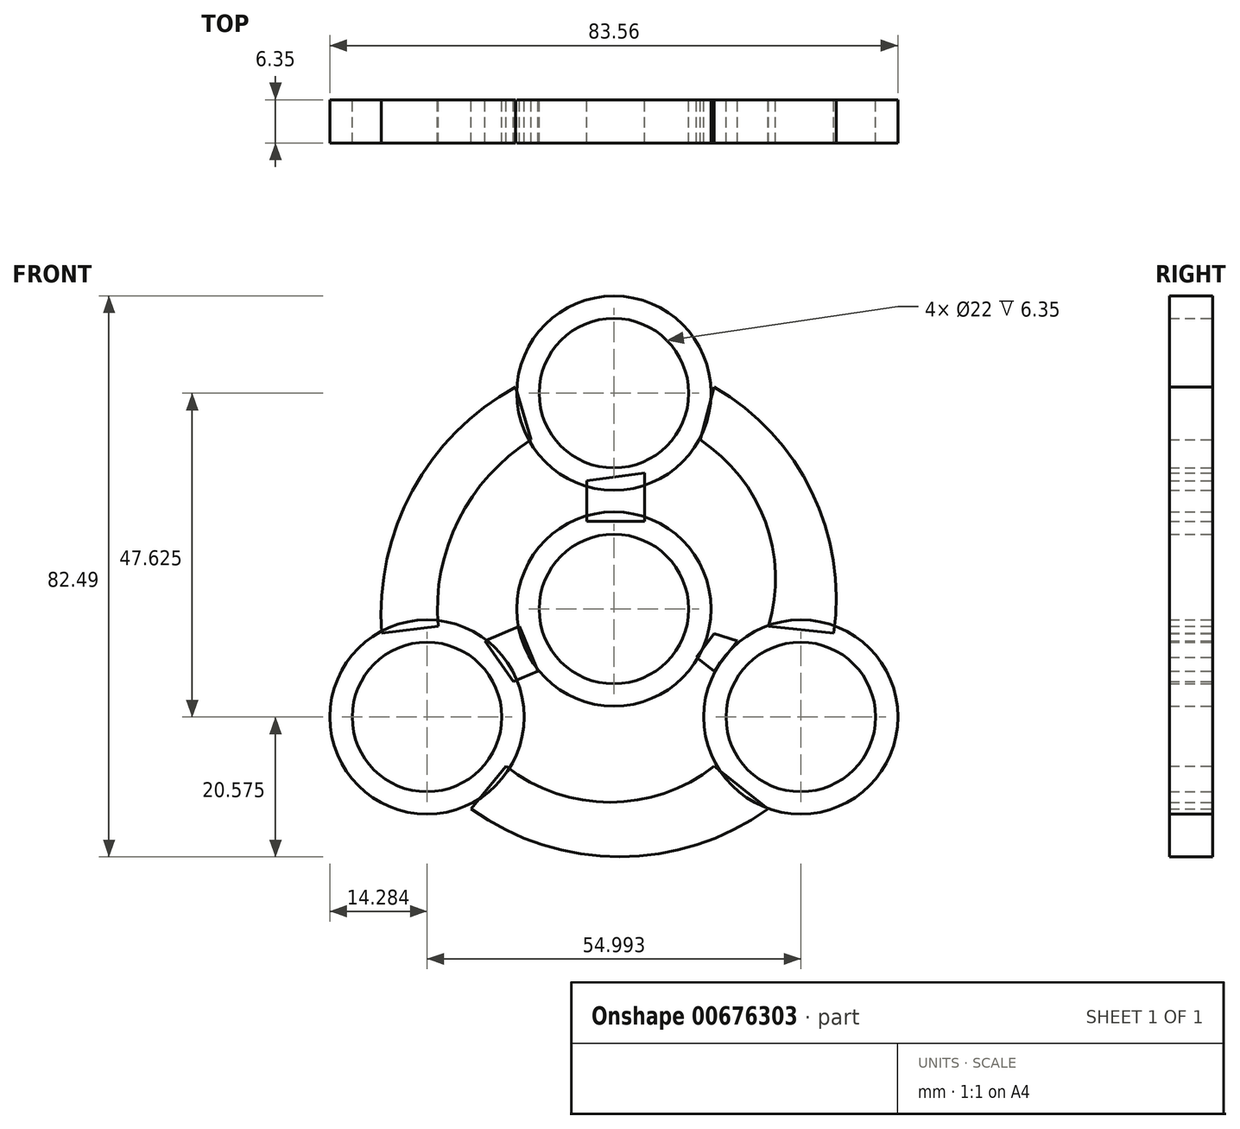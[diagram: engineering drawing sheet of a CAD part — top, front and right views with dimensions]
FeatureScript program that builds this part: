
annotation { "Feature Type Name" : "Feature", "Feature Type Description" : "" }
export const myFeature = defineFeature(function(context is Context, id is Id, definition is map)
    precondition{}
    {
        {
            var Q0;
            Q0=qCreatedBy(makeId("Front.planeOp"),FACE);
            var sketch = newSketch(context, id + "F0", { "sketchPlane" : qUnion([Q0])});
            skCircle(sketch, "E0", {"center": v(0, 0) * mm, "radius": 14.29 * mm});
            skCircle(sketch, "E1", {"center": v(0, 0) * mm, "radius": 11 * mm});
            skLineSegment(sketch, "E2", {"start": v(0, 0) * mm, "end": v(0, 31.75) * mm});
            skCircle(sketch, "E3", {"center": v(0, 31.75) * mm, "radius": 14.29 * mm});
            skCircle(sketch, "E4", {"center": v(0, 31.75) * mm, "radius": 11 * mm});
            skCircle(sketch, "E5.1.0", {"center": v(-27.5, -15.87) * mm, "radius": 14.29 * mm});
            skCircle(sketch, "E5.1.1", {"center": v(-27.5, -15.87) * mm, "radius": 11 * mm});
            skCircle(sketch, "E5.2.0", {"center": v(27.5, -15.88) * mm, "radius": 14.29 * mm});
            skCircle(sketch, "E5.2.1", {"center": v(27.5, -15.88) * mm, "radius": 11 * mm});
            skSolve(sketch);
        }
        {
            var Q0;
            Q0=qCreatedBy(makeId("Front.planeOp"),FACE);
            var sketch = newSketch(context, id + "F1", { "sketchPlane" : qUnion([Q0])});
            skArc(sketch, "E6", {"start": v(-14.49, 32.64) * mm, "mid": v(-29.64, 17.42) * mm, "end": v(-34.15, -3.57) * mm});
            skArc(sketch, "E7", {"start": v(-12.16, 24.88) * mm, "mid": v(-22.86, 13.1) * mm, "end": v(-25.87, -2.54) * mm});
            skArc(sketch, "E8", {"start": v(22.76, -2.54) * mm, "mid": v(22.29, 12.85) * mm, "end": v(12.68, 24.88) * mm});
            skArc(sketch, "E9", {"start": v(32.33, -3.57) * mm, "mid": v(29.11, 17.24) * mm, "end": v(14.74, 32.64) * mm});
            skArc(sketch, "E10", {"start": v(-15.89, -23.12) * mm, "mid": v(-0.57, -28.42) * mm, "end": v(14.75, -23.12) * mm});
            skArc(sketch, "E11", {"start": v(-21, -29.37) * mm, "mid": v(0.85, -36.45) * mm, "end": v(22.7, -29.37) * mm});
            skLineSegment(sketch, "E12", {"start": v(-3.97, 18.87) * mm, "end": v(-3.97, 12.9) * mm});
            skLineSegment(sketch, "E13", {"start": v(-3.97, 12.9) * mm, "end": v(4.54, 12.9) * mm});
            skLineSegment(sketch, "E14", {"start": v(4.54, 12.9) * mm, "end": v(4.54, 20) * mm});
            skLineSegment(sketch, "E15", {"start": v(4.54, 20) * mm, "end": v(-3.97, 18.87) * mm});
            skLineSegment(sketch, "E16", {"start": v(-19, -4.68) * mm, "end": v(-13.9, -2.54) * mm});
            skLineSegment(sketch, "E17", {"start": v(-13.9, -2.54) * mm, "end": v(-11.14, -9.12) * mm});
            skLineSegment(sketch, "E18", {"start": v(-11.14, -9.12) * mm, "end": v(-14.8, -10.65) * mm});
            skLineSegment(sketch, "E19", {"start": v(-14.8, -10.65) * mm, "end": v(-19, -4.68) * mm});
            skLineSegment(sketch, "E20", {"start": v(14.75, -3.61) * mm, "end": v(18.16, -4.68) * mm});
            skLineSegment(sketch, "E21", {"start": v(18.16, -4.68) * mm, "end": v(14.75, -9.12) * mm});
            skLineSegment(sketch, "E22", {"start": v(14.75, -9.12) * mm, "end": v(12.16, -7.12) * mm});
            skLineSegment(sketch, "E23", {"start": v(12.16, -7.12) * mm, "end": v(14.75, -3.61) * mm});
            skLineSegment(sketch, "E24", {"start": v(-34.15, -3.57) * mm, "end": v(-25.87, -2.54) * mm});
            skLineSegment(sketch, "E25", {"start": v(-14.49, 32.64) * mm, "end": v(-12.16, 24.88) * mm});
            skLineSegment(sketch, "E26", {"start": v(12.68, 24.88) * mm, "end": v(14.74, 32.64) * mm});
            skLineSegment(sketch, "E27", {"start": v(22.76, -2.54) * mm, "end": v(32.33, -3.57) * mm});
            skLineSegment(sketch, "E28", {"start": v(-21, -29.37) * mm, "end": v(-15.89, -23.12) * mm});
            skLineSegment(sketch, "E29", {"start": v(14.75, -23.12) * mm, "end": v(22.7, -29.37) * mm});
            skSolve(sketch);
        }
        {
            var Q0;
            Q0=makeQuery(id+"F1.imprint","IMPRINT",FACE,{"disambiguationData":[TD([[makeQuery(id+"F1.imprint","IMPRINT",EDGE,{"derivedFrom":sQuery(id+"F1.wireOp",EDGE,"E6")}),1.0]])]});
            var Q1;
            Q1=makeQuery(id+"F1.imprint","IMPRINT",FACE,{"disambiguationData":[TD([[makeQuery(id+"F1.imprint","IMPRINT",EDGE,{"derivedFrom":sQuery(id+"F1.wireOp",EDGE,"E8")}),-1.0]])]});
            var Q2;
            Q2=makeQuery(id+"F0.imprint","IMPRINT",FACE,{"disambiguationData":[TD([[makeQuery(id+"F0.imprint","IMPRINT",EDGE,{"derivedFrom":sQuery(id+"F0.wireOp",EDGE,"E5.2.0")}),1.0]])]});
            var Q3;
            Q3=makeQuery(id+"F1.imprint","IMPRINT",FACE,{"disambiguationData":[TD([[makeQuery(id+"F1.imprint","IMPRINT",EDGE,{"derivedFrom":sQuery(id+"F1.wireOp",EDGE,"E20")}),-1.0]])]});
            var Q4;
            Q4=makeQuery(id+"F0.imprint","IMPRINT",FACE,{"disambiguationData":[TD([[makeQuery(id+"F0.imprint","IMPRINT",EDGE,{"derivedFrom":sQuery(id+"F0.wireOp",EDGE,"E0")}),1.0]])]});
            var Q5;
            Q5=makeQuery(id+"F1.imprint","IMPRINT",FACE,{"disambiguationData":[TD([[makeQuery(id+"F1.imprint","IMPRINT",EDGE,{"derivedFrom":sQuery(id+"F1.wireOp",EDGE,"E12")}),1.0]])]});
            var Q6;
            Q6=makeQuery(id+"F0.imprint","IMPRINT",FACE,{"disambiguationData":[TD([[makeQuery(id+"F0.imprint","IMPRINT",EDGE,{"derivedFrom":sQuery(id+"F0.wireOp",EDGE,"E3")}),1.0]])]});
            var Q7;
            Q7=makeQuery(id+"F1.imprint","IMPRINT",FACE,{"disambiguationData":[TD([[makeQuery(id+"F1.imprint","IMPRINT",EDGE,{"derivedFrom":sQuery(id+"F1.wireOp",EDGE,"E16")}),-1.0]])]});
            var Q8;
            Q8=makeQuery(id+"F0.imprint","IMPRINT",FACE,{"disambiguationData":[TD([[makeQuery(id+"F0.imprint","IMPRINT",EDGE,{"derivedFrom":sQuery(id+"F0.wireOp",EDGE,"E5.1.0")}),1.0]])]});
            var Q9;
            Q9=makeQuery(id+"F1.imprint","IMPRINT",FACE,{"disambiguationData":[TD([[makeQuery(id+"F1.imprint","IMPRINT",EDGE,{"derivedFrom":sQuery(id+"F1.wireOp",EDGE,"E10")}),-1.0]])]});
            extrude(context, id + "F2", {"entities" : qUnion([Q0, Q1, Q2, Q3, Q4, Q5, Q6, Q7, Q8, Q9]), "depth" : 25.4 * mm, "offsetDistance" : 25.4 * mm});
        }
        {
            var Q0;
            Q0=makeQuery(id+"F2.opExtrude","CAP_FACE",FACE,{"disambiguationData":[OSD([sQuery(id+"F1.wireOp",EDGE,"E6"),sQuery(id+"F1.wireOp",EDGE,"E7"),sQuery(id+"F1.wireOp",EDGE,"E24"),sQuery(id+"F1.wireOp",EDGE,"E25")])],"isStart":false});
            var Q1;
            Q1=makeQuery(id+"F2.opExtrude","CAP_FACE",FACE,{"disambiguationData":[OSD([sQuery(id+"F0.wireOp",EDGE,"E5.1.0"),sQuery(id+"F0.wireOp",EDGE,"E5.1.1")])],"isStart":false});
            var Q2;
            Q2=makeQuery(id+"F2.opExtrude","CAP_FACE",FACE,{"disambiguationData":[OSD([sQuery(id+"F0.wireOp",EDGE,"E0"),sQuery(id+"F0.wireOp",EDGE,"E1")])],"isStart":false});
            var Q3;
            Q3=makeQuery(id+"F2.opExtrude","CAP_FACE",FACE,{"disambiguationData":[OSD([sQuery(id+"F1.wireOp",EDGE,"E16"),sQuery(id+"F1.wireOp",EDGE,"E17"),sQuery(id+"F1.wireOp",EDGE,"E18"),sQuery(id+"F1.wireOp",EDGE,"E19")])],"isStart":false});
            var Q4;
            Q4=makeQuery(id+"F2.opExtrude","CAP_FACE",FACE,{"disambiguationData":[OSD([sQuery(id+"F1.wireOp",EDGE,"E10"),sQuery(id+"F1.wireOp",EDGE,"E11"),sQuery(id+"F1.wireOp",EDGE,"E28"),sQuery(id+"F1.wireOp",EDGE,"E29")])],"isStart":false});
            var Q5;
            Q5=makeQuery(id+"F2.opExtrude","CAP_FACE",FACE,{"disambiguationData":[OSD([sQuery(id+"F0.wireOp",EDGE,"E5.2.0"),sQuery(id+"F0.wireOp",EDGE,"E5.2.1")])],"isStart":false});
            var Q6;
            Q6=makeQuery(id+"F2.opExtrude","CAP_FACE",FACE,{"disambiguationData":[OSD([sQuery(id+"F1.wireOp",EDGE,"E20"),sQuery(id+"F1.wireOp",EDGE,"E21"),sQuery(id+"F1.wireOp",EDGE,"E22"),sQuery(id+"F1.wireOp",EDGE,"E23")])],"isStart":false});
            var Q7;
            Q7=makeQuery(id+"F2.opExtrude","CAP_FACE",FACE,{"disambiguationData":[OSD([sQuery(id+"F0.wireOp",EDGE,"E3"),sQuery(id+"F0.wireOp",EDGE,"E4")])],"isStart":false});
            var Q8;
            Q8=makeQuery(id+"F2.opExtrude","CAP_FACE",FACE,{"disambiguationData":[OSD([sQuery(id+"F1.wireOp",EDGE,"E12"),sQuery(id+"F1.wireOp",EDGE,"E13"),sQuery(id+"F1.wireOp",EDGE,"E14"),sQuery(id+"F1.wireOp",EDGE,"E15")])],"isStart":false});
            var Q9;
            Q9=makeQuery(id+"F2.opExtrude","CAP_FACE",FACE,{"disambiguationData":[OSD([sQuery(id+"F1.wireOp",EDGE,"E8"),sQuery(id+"F1.wireOp",EDGE,"E9"),sQuery(id+"F1.wireOp",EDGE,"E26"),sQuery(id+"F1.wireOp",EDGE,"E27")])],"isStart":false});
            extrude(context, id + "F3", {"entities" : qUnion([Q0, Q1, Q2, Q3, Q4, Q5, Q6, Q7, Q8, Q9]), "operationType" : NewBodyOperationType.REMOVE, "oppositeDirection" : true, "depth" : 19.05 * mm, "offsetDistance" : 25.4 * mm});
        }
    });
